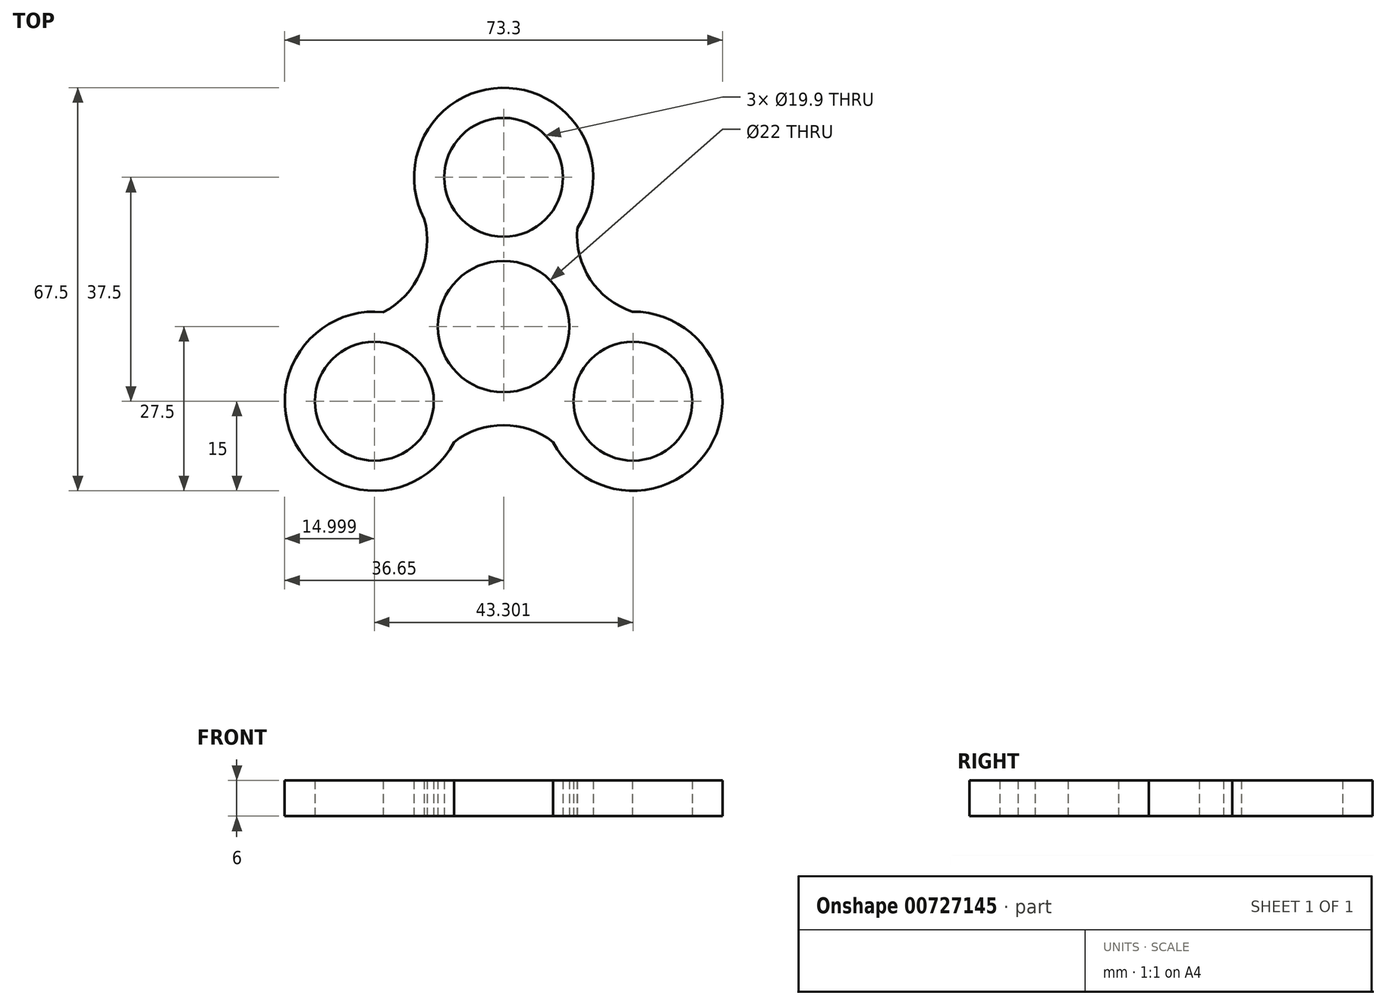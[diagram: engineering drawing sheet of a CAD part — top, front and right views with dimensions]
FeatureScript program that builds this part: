
annotation { "Feature Type Name" : "Feature", "Feature Type Description" : "" }
export const myFeature = defineFeature(function(context is Context, id is Id, definition is map)
    precondition{}
    {
        {
            var Q0;
            Q0=qCreatedBy(makeId("Top.planeOp"),FACE);
            var sketch = newSketch(context, id + "F0", { "sketchPlane" : qUnion([Q0])});
            skCircle(sketch, "E0", {"center": v(0, 0) * mm, "radius": 11 * mm});
            skLineSegment(sketch, "E1", {"start": v(0, 0) * mm, "end": v(0, 14) * mm});
            skArc(sketch, "E2", {"start": v(12.34, 16.48) * mm, "mid": v(0.91, 39.97) * mm, "end": v(-13.29, 18.04) * mm});
            skArc(sketch, "E3.1.0", {"start": v(-20.14, 2.42) * mm, "mid": v(-34.83, -19.66) * mm, "end": v(-8.31, -19.36) * mm});
            skArc(sketch, "E3.2.0", {"start": v(8.31, -19.36) * mm, "mid": v(34.48, -20.27) * mm, "end": v(21.56, 2.5) * mm});
            skCircle(sketch, "E4", {"center": v(0, 25) * mm, "radius": 9.95 * mm});
            skCircle(sketch, "E5", {"center": v(21.65, -12.5) * mm, "radius": 9.95 * mm});
            skCircle(sketch, "E6", {"center": v(-21.65, -12.5) * mm, "radius": 9.95 * mm});
            skLineSegment(sketch, "E7", {"start": v(0, 0) * mm, "end": v(0, -15) * mm});
            skArc(sketch, "E8", {"start": v(12.34, 16.48) * mm, "mid": v(14.52, 7.89) * mm, "end": v(21.56, 2.5) * mm});
            skArc(sketch, "E9", {"start": v(-20.14, 2.42) * mm, "mid": v(-13.94, 9.01) * mm, "end": v(-13.29, 18.04) * mm});
            skArc(sketch, "E10", {"start": v(8.31, -19.36) * mm, "mid": v(0, -16.5) * mm, "end": v(-8.31, -19.36) * mm});
            skPoint(sketch, "E11.orphan", {"position": v(8.3, 12.5) * mm});
            skPoint(sketch, "E12.orphan", {"position": v(14.97, 0.93) * mm});
            skPoint(sketch, "E13.orphan", {"position": v(-6.68, -13.43) * mm});
            skSolve(sketch);
        }
        {
            var Q0;
            Q0 = qSketchRegion(id + "F0", true);
            extrude(context, id + "F1", {"entities" : qUnion([Q0]), "depth" : 6 * mm, "offsetDistance" : 25 * mm});
        }
    });
